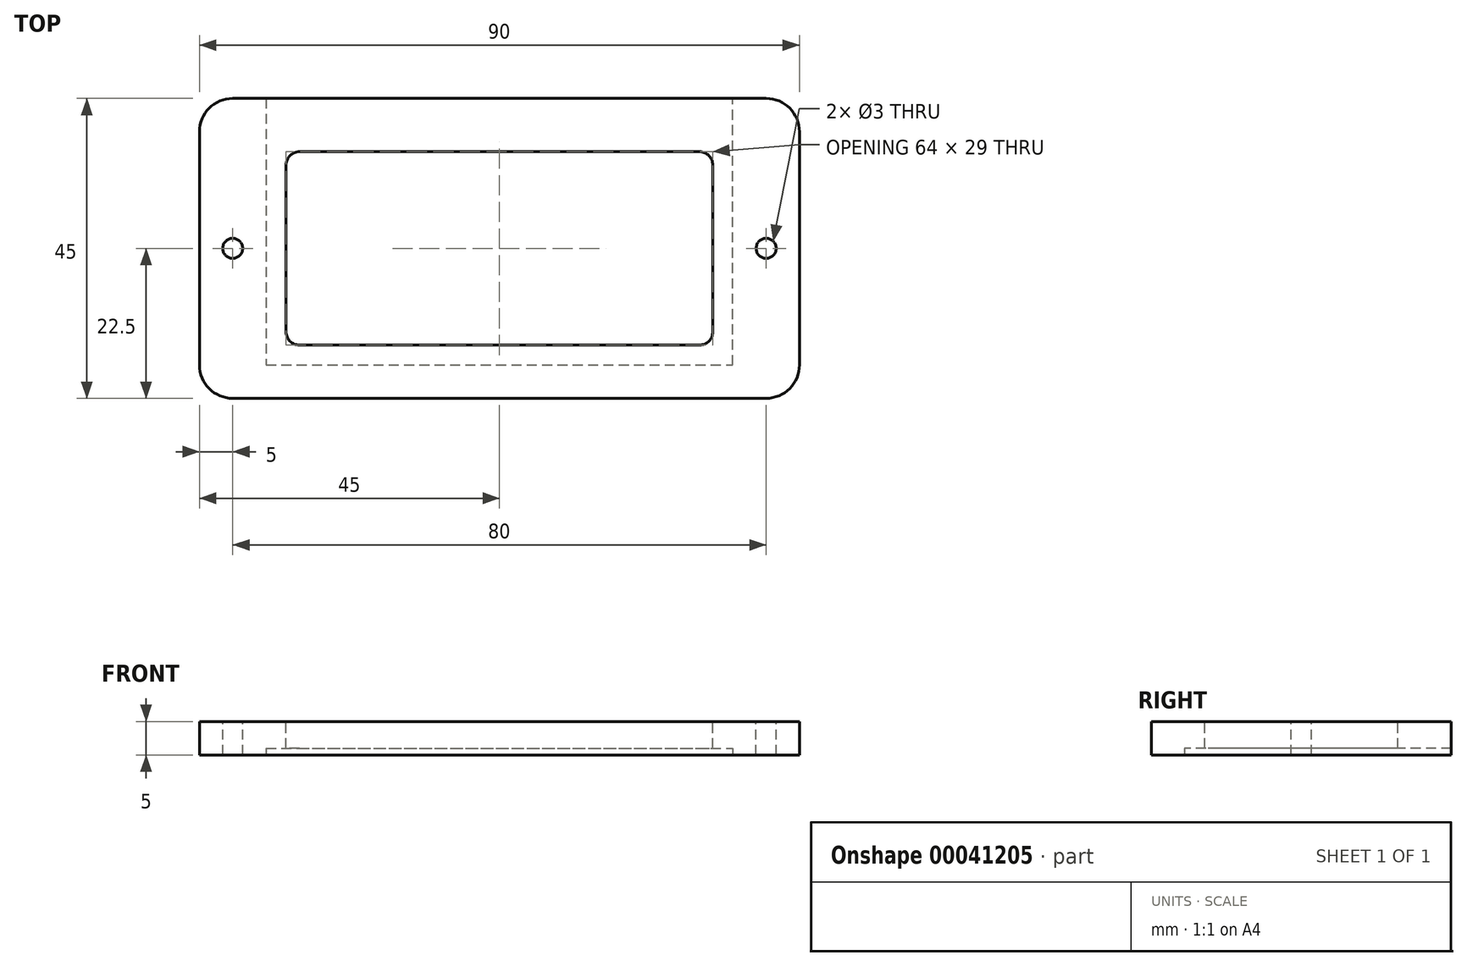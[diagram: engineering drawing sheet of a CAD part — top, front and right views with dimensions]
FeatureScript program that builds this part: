
annotation { "Feature Type Name" : "Feature", "Feature Type Description" : "" }
export const myFeature = defineFeature(function(context is Context, id is Id, definition is map)
    precondition{}
    {
        {
            var Q0;
            Q0=qCreatedBy(makeId("Top.planeOp"),FACE);
            var sketch = newSketch(context, id + "F0", { "sketchPlane" : qUnion([Q0])});
            skLineSegment(sketch, "E0.bottom", {"start": v(0, 0) * mm, "end": v(90, 0) * mm});
            skLineSegment(sketch, "E0.top", {"start": v(0, 45) * mm, "end": v(90, 45) * mm});
            skLineSegment(sketch, "E0.left", {"start": v(0, 0) * mm, "end": v(0, 45) * mm});
            skLineSegment(sketch, "E0.right", {"start": v(90, 0) * mm, "end": v(90, 45) * mm});
            skSolve(sketch);
        }
        {
            var Q0;
            Q0 = qSketchRegion(id + "F0", true);
            extrude(context, id + "F1", {"entities" : qUnion([Q0]), "depth" : 5 * mm});
        }
        {
            var Q0;
            Q0=makeQuery(id+"F1.opExtrude","SWEPT_EDGE",EDGE,{"disambiguationData":[OSD([sQuery(id+"F0.wireOp",EDGE,"E0.top"),sQuery(id+"F0.wireOp",EDGE,"E0.right")])]});
            var Q1;
            Q1=makeQuery(id+"F1.opExtrude","SWEPT_EDGE",EDGE,{"disambiguationData":[OSD([sQuery(id+"F0.wireOp",EDGE,"E0.bottom"),sQuery(id+"F0.wireOp",EDGE,"E0.right")])]});
            var Q2;
            Q2=makeQuery(id+"F1.opExtrude","SWEPT_EDGE",EDGE,{"disambiguationData":[OSD([sQuery(id+"F0.wireOp",EDGE,"E0.top"),sQuery(id+"F0.wireOp",EDGE,"E0.left")])]});
            var Q3;
            Q3=makeQuery(id+"F1.opExtrude","SWEPT_EDGE",EDGE,{"disambiguationData":[OSD([sQuery(id+"F0.wireOp",EDGE,"E0.bottom"),sQuery(id+"F0.wireOp",EDGE,"E0.left")])]});
            fillet(context, id + "F2", {"entities" : qUnion([Q0, Q1, Q2, Q3]), "radius" : 5 * mm, "tangentPropagation" : true, "allowEdgeOverflow" : false});
        }
        {
            var Q0;
            Q0=qCreatedBy(makeId("Top.planeOp"),FACE);
            var sketch = newSketch(context, id + "F3", { "sketchPlane" : qUnion([Q0])});
            skLineSegment(sketch, "E1", {"start": v(10, 45) * mm, "end": v(10, 5) * mm});
            skLineSegment(sketch, "E2", {"start": v(10, 5) * mm, "end": v(80, 5) * mm});
            skLineSegment(sketch, "E3", {"start": v(80, 5) * mm, "end": v(80, 45) * mm});
            skLineSegment(sketch, "E4.0", {"start": v(10, 45) * mm, "end": v(80, 45) * mm});
            skPoint(sketch, "E5.orphan", {"position": v(5, 45) * mm});
            skPoint(sketch, "E6.orphan", {"position": v(85, 45) * mm});
            skPoint(sketch, "E7.orphan", {"position": v(99.44, 5) * mm});
            skSolve(sketch);
        }
        {
            var Q0;
            Q0 = qSketchRegion(id + "F3", true);
            extrude(context, id + "F4", {"entities" : qUnion([Q0]), "operationType" : NewBodyOperationType.REMOVE, "depth" : 1 * mm});
        }
        {
            var Q0;
            Q0=makeQuery(id+"F1.opExtrude","CAP_FACE",FACE,{"disambiguationData":[OSD([sQuery(id+"F0.wireOp",EDGE,"E0.bottom"),sQuery(id+"F0.wireOp",EDGE,"E0.top"),sQuery(id+"F0.wireOp",EDGE,"E0.left"),sQuery(id+"F0.wireOp",EDGE,"E0.right")])],"isStart":false});
            var sketch = newSketch(context, id + "F5", { "sketchPlane" : qUnion([Q0])});
            skLineSegment(sketch, "E8.bottom", {"start": v(15, 37) * mm, "end": v(75, 37) * mm});
            skLineSegment(sketch, "E8.top", {"start": v(15, 8) * mm, "end": v(75, 8) * mm});
            skLineSegment(sketch, "E8.left", {"start": v(13, 35) * mm, "end": v(13, 10) * mm});
            skLineSegment(sketch, "E8.right", {"start": v(77, 35) * mm, "end": v(77, 10) * mm});
            skPoint(sketch, "E9.visualSharp", {"position": v(13, 37) * mm});
            skArc(sketch, "E9.filletArc", {"start": v(15, 37) * mm, "mid": v(13.59, 36.41) * mm, "end": v(13, 35) * mm});
            skPoint(sketch, "E10.visualSharp", {"position": v(13, 8) * mm});
            skArc(sketch, "E10.filletArc", {"start": v(13, 10) * mm, "mid": v(13.59, 8.59) * mm, "end": v(15, 8) * mm});
            skPoint(sketch, "E11.visualSharp", {"position": v(77, 8) * mm});
            skArc(sketch, "E11.filletArc", {"start": v(75, 8) * mm, "mid": v(76.41, 8.59) * mm, "end": v(77, 10) * mm});
            skPoint(sketch, "E12.visualSharp", {"position": v(77, 37) * mm});
            skArc(sketch, "E12.filletArc", {"start": v(77, 35) * mm, "mid": v(76.41, 36.41) * mm, "end": v(75, 37) * mm});
            skSolve(sketch);
        }
        {
            var Q0;
            Q0 = qSketchRegion(id + "F5", true);
            extrude(context, id + "F6", {"entities" : qUnion([Q0]), "operationType" : NewBodyOperationType.REMOVE, "oppositeDirection" : true, "depth" : 25 * mm});
        }
        {
            var Q0;
            Q0=makeQuery(id+"F1.opExtrude","CAP_FACE",FACE,{"disambiguationData":[OSD([sQuery(id+"F0.wireOp",EDGE,"E0.bottom"),sQuery(id+"F0.wireOp",EDGE,"E0.top"),sQuery(id+"F0.wireOp",EDGE,"E0.left"),sQuery(id+"F0.wireOp",EDGE,"E0.right")])],"isStart":false});
            var sketch = newSketch(context, id + "F7", { "sketchPlane" : qUnion([Q0])});
            skLineSegment(sketch, "E13", {"start": v(0, 22.5) * mm, "end": v(5, 22.5) * mm, "construction": true});
            skLineSegment(sketch, "E14", {"start": v(90, 22.5) * mm, "end": v(85, 22.5) * mm, "construction": true});
            skCircle(sketch, "E15", {"center": v(5, 22.5) * mm, "radius": 1.5 * mm});
            skCircle(sketch, "E16", {"center": v(85, 22.5) * mm, "radius": 1.5 * mm});
            skSolve(sketch);
        }
        {
            var Q0;
            Q0 = qSketchRegion(id + "F7", true);
            extrude(context, id + "F8", {"entities" : qUnion([Q0]), "operationType" : NewBodyOperationType.REMOVE, "oppositeDirection" : true, "depth" : 25 * mm});
        }
    });
